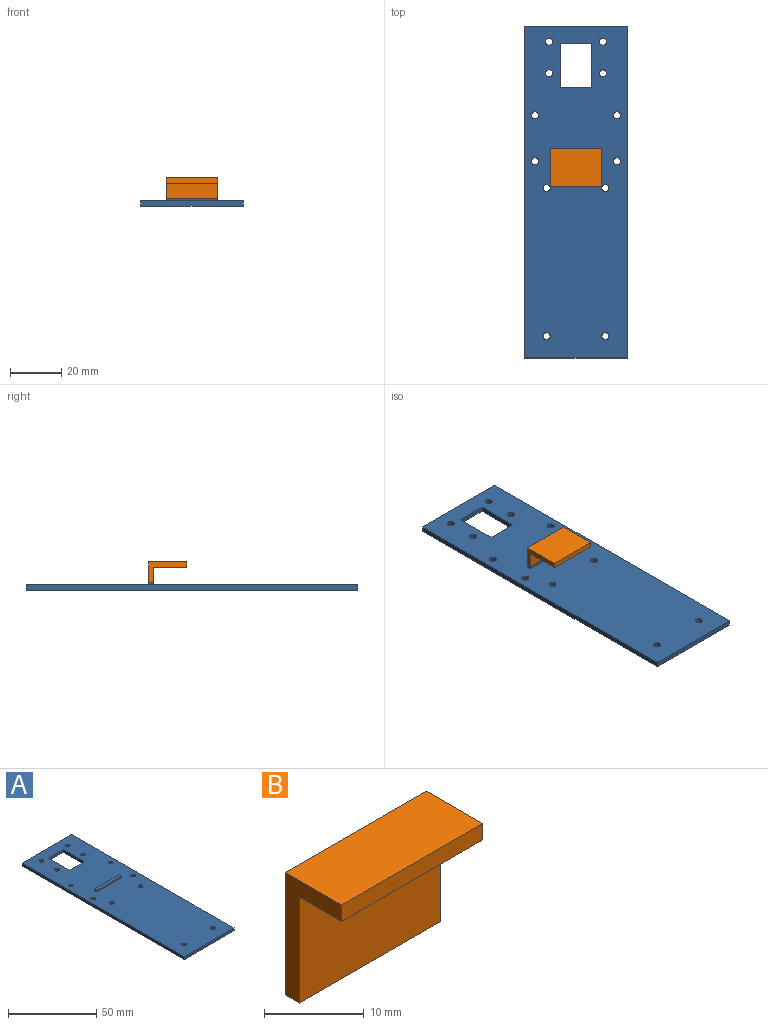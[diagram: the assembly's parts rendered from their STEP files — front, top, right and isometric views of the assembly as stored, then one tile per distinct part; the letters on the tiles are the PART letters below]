
ASSEMBLY  parts=2 mates=1
PART A: 27 faces, bbox 40x130x3 mm
  f0: plane 130x40mm, normal (0,0,1), area 4884.7mm2, adj f1,f2,f3,f4,f5,f6,f7,f8
  f1: plane 12x2mm, normal (0,-1,0), area 24mm2, adj f0,f2,f13,f21
  f2: plane 17x2mm, normal (-1,0,0), area 34mm2, adj f0,f1,f3,f21
  f3: plane 12x2mm, normal (0,1,0), area 24mm2, adj f0,f2,f13,f21
  f4: plane 130x2mm, normal (-1,0,0), area 260mm2, adj f0,f5,f19,f21
  f5: plane 40x2mm, normal (0,-1,0), area 80mm2, adj f0,f4,f6,f21
  f6: plane 130x2mm, normal (1,0,0), area 260mm2, adj f0,f5,f19,f21
  f7: cylinder r=1.38mm len=2.75mm, axis (0,0,-1), area 17.3mm2, adj f0,f21
  f8: cylinder r=1.38mm len=2.75mm, axis (0,0,-1), area 17.3mm2, adj f0,f21
  f9: cylinder r=1.38mm len=2.75mm, axis (0,0,-1), area 17.3mm2, adj f0,f21
  f10: cylinder r=1.38mm len=2.75mm, axis (0,0,-1), area 17.3mm2, adj f0,f21
  f11: cylinder r=1.38mm len=2.75mm, axis (0,0,-1), area 17.3mm2, adj f0,f21
  f12: cylinder r=1.38mm len=2.75mm, axis (0,0,-1), area 17.3mm2, adj f0,f21
  f13: plane 17x2mm, normal (1,0,0), area 34mm2, adj f0,f1,f3,f21
  f14: cylinder r=1.38mm len=2.75mm, axis (0,0,-1), area 17.3mm2, adj f0,f21
  f15: cylinder r=1.38mm len=2.75mm, axis (0,0,-1), area 17.3mm2, adj f0,f21
  f16: cylinder r=1.38mm len=2.75mm, axis (0,0,-1), area 17.3mm2, adj f0,f21
  f17: cylinder r=1.38mm len=2.75mm, axis (0,0,-1), area 17.3mm2, adj f0,f21
  f18: cylinder r=1.38mm len=2.75mm, axis (0,0,-1), area 17.3mm2, adj f0,f21
  f19: plane 40x2mm, normal (0,1,0), area 80mm2, adj f0,f4,f6,f21
  f20: cylinder r=1.38mm len=2.75mm, axis (0,0,-1), area 17.3mm2, adj f0,f21
  f21: plane 130x40mm, normal (0,0,-1), area 4924.7mm2, adj f1,f2,f3,f4,f5,f6,f7,f8
  f22: plane 20x1mm, normal (0,-1,0), area 20mm2, adj f0,f23,f25,f26
  f23: plane 2x1mm, normal (1,0,0), area 2mm2, adj f0,f22,f24,f26
  f24: plane 20x1mm, normal (0,1,0), area 20mm2, adj f0,f23,f25,f26
  f25: plane 2x1mm, normal (-1,0,0), area 2mm2, adj f0,f22,f24,f26
  f26: plane 20x2mm, normal (0,0,1), area 40mm2, adj f22,f23,f24,f25
PART B: 8 faces, bbox 20x8x15 mm
  f0: plane 20x15mm, normal (0,1,0), area 300mm2, adj f1,f5,f6,f7
  f1: plane 20x8mm, normal (0,0,1), area 160mm2, adj f0,f2,f6,f7
  f2: plane 20x2mm, normal (0,-1,0), area 40mm2, adj f1,f3,f6,f7
  f3: plane 20x6mm, normal (0,0,-1), area 120mm2, adj f2,f4,f6,f7
  f4: plane 20x13mm, normal (0,-1,0), area 260mm2, adj f3,f5,f6,f7
  f5: plane 20x2mm, normal (0,0,-1), area 40mm2, adj f0,f4,f6,f7
  f6: plane 15x8mm, normal (1,0,0), area 42mm2, adj f0,f1,f2,f3,f4,f5
  f7: plane 15x8mm, normal (-1,0,0), area 42mm2, adj f0,f1,f2,f3,f4,f5
PLACE A t=(-23.55,32.91,5.78)mm
PLACE B rot(axis=(0,0.71,0.71),180deg) t=(-13.55,49.95,9.58)mm
MATE fastened B.f2 <-> A.f26  axis (0,0,-1) through (-23.55,49.95,8.78)mm
